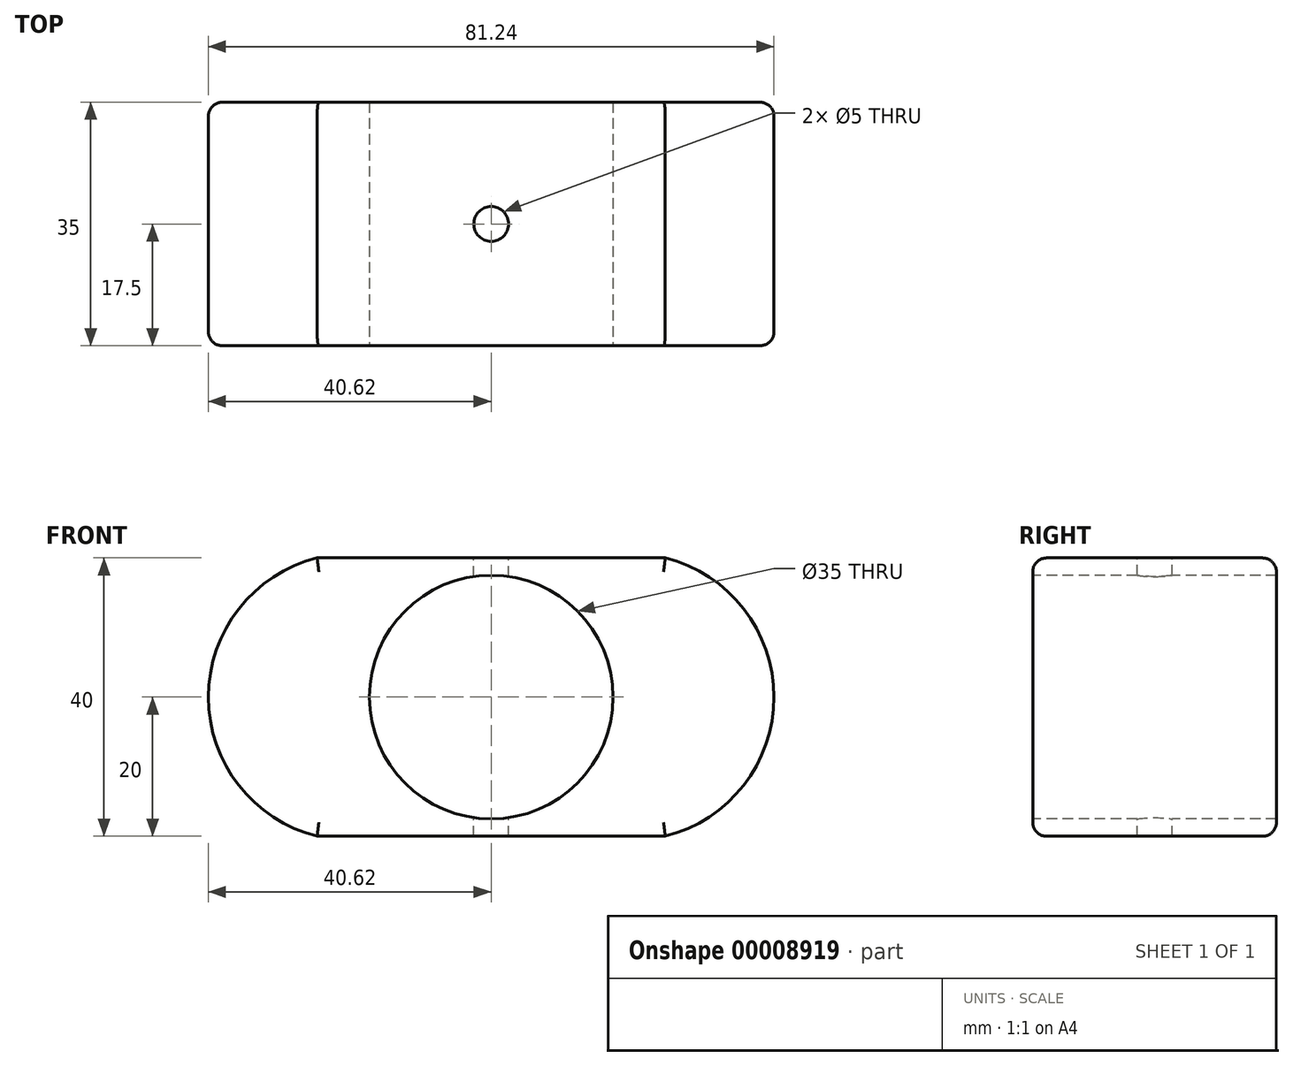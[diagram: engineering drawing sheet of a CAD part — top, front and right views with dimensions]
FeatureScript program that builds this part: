
annotation { "Feature Type Name" : "Feature", "Feature Type Description" : "" }
export const myFeature = defineFeature(function(context is Context, id is Id, definition is map)
    precondition{}
    {
        {
            var Q0;
            Q0=qCreatedBy(makeId("Front.planeOp"),FACE);
            var sketch = newSketch(context, id + "F0", { "sketchPlane" : qUnion([Q0])});
            skLineSegment(sketch, "E0.bottom", {"start": v(0, 0) * mm, "end": v(-50, 0) * mm});
            skLineSegment(sketch, "E0.top", {"start": v(0, 40) * mm, "end": v(-50, 40) * mm});
            skLineSegment(sketch, "E0.left", {"start": v(0, 0) * mm, "end": v(0, 40) * mm});
            skLineSegment(sketch, "E0.right", {"start": v(-50, 0) * mm, "end": v(-50, 40) * mm});
            skArc(sketch, "E1", {"start": v(0, 0) * mm, "mid": v(15.62, 20) * mm, "end": v(0, 40) * mm});
            skArc(sketch, "E2", {"start": v(-50, 40) * mm, "mid": v(-65.62, 20) * mm, "end": v(-50, 0) * mm});
            skSolve(sketch);
        }
        {
            var Q0;
            Q0 = qSketchRegion(id + "F0", true);
            extrude(context, id + "F1", {"entities" : qUnion([Q0]), "depth" : 35 * mm});
        }
        {
            var Q0;
            Q0=makeQuery(id+"F1.opExtrude","CAP_FACE",FACE,{"disambiguationData":[OSD([sQuery(id+"F0.wireOp",EDGE,"E0.bottom"),sQuery(id+"F0.wireOp",EDGE,"E0.top"),sQuery(id+"F0.wireOp",EDGE,"E1"),sQuery(id+"F0.wireOp",EDGE,"E2")])],"isStart":false});
            var sketch = newSketch(context, id + "F2", { "sketchPlane" : qUnion([Q0])});
            skCircle(sketch, "E3", {"center": v(-25, 20) * mm, "radius": 17.5 * mm});
            skSolve(sketch);
        }
        {
            var Q0;
            Q0 = qSketchRegion(id + "F2", true);
            extrude(context, id + "F3", {"entities" : qUnion([Q0]), "operationType" : NewBodyOperationType.REMOVE, "oppositeDirection" : true, "depth" : 35 * mm});
        }
        {
            var Q0;
            Q0=makeQuery(id+"F1.opExtrude","SWEPT_FACE",FACE,{"disambiguationData":[OSD([sQuery(id+"F0.wireOp",EDGE,"E0.top")])]});
            var sketch = newSketch(context, id + "F4", { "sketchPlane" : qUnion([Q0])});
            skCircle(sketch, "E4", {"center": v(-25, -17.5) * mm, "radius": 2.5 * mm});
            skSolve(sketch);
        }
        {
            var Q0;
            Q0 = qSketchRegion(id + "F4", true);
            extrude(context, id + "F5", {"entities" : qUnion([Q0]), "operationType" : NewBodyOperationType.REMOVE, "endBound" : BoundingType.THROUGH_ALL, "oppositeDirection" : true, "depth" : 25 * mm});
        }
        {
            var Q0;
            Q0=makeQuery(id+"F1.opExtrude","CAP_EDGE",EDGE,{"disambiguationData":[OSD([sQuery(id+"F0.wireOp",EDGE,"E0.top")])],"isStart":false});
            var Q1;
            Q1=makeQuery(id+"F1.opExtrude","CAP_EDGE",EDGE,{"disambiguationData":[OSD([sQuery(id+"F0.wireOp",EDGE,"E0.bottom")])],"isStart":false});
            var Q2;
            Q2=makeQuery(id+"F1.opExtrude","CAP_EDGE",EDGE,{"disambiguationData":[OSD([sQuery(id+"F0.wireOp",EDGE,"E2")])],"isStart":false});
            var Q3;
            Q3=makeQuery(id+"F1.opExtrude","CAP_EDGE",EDGE,{"disambiguationData":[OSD([sQuery(id+"F0.wireOp",EDGE,"E1")])],"isStart":false});
            var Q4;
            Q4=makeQuery(id+"F1.opExtrude","CAP_EDGE",EDGE,{"disambiguationData":[OSD([sQuery(id+"F0.wireOp",EDGE,"E0.top")])],"isStart":true});
            var Q5;
            Q5=makeQuery(id+"F1.opExtrude","CAP_EDGE",EDGE,{"disambiguationData":[OSD([sQuery(id+"F0.wireOp",EDGE,"E2")])],"isStart":true});
            var Q6;
            Q6=makeQuery(id+"F1.opExtrude","CAP_EDGE",EDGE,{"disambiguationData":[OSD([sQuery(id+"F0.wireOp",EDGE,"E1")])],"isStart":true});
            var Q7;
            Q7=makeQuery(id+"F1.opExtrude","CAP_EDGE",EDGE,{"disambiguationData":[OSD([sQuery(id+"F0.wireOp",EDGE,"E0.bottom")])],"isStart":true});
            fillet(context, id + "F6", {"entities" : qUnion([Q0, Q1, Q2, Q3, Q4, Q5, Q6, Q7]), "radius" : 2 * mm, "tangentPropagation" : true, "allowEdgeOverflow" : false});
        }
    });
